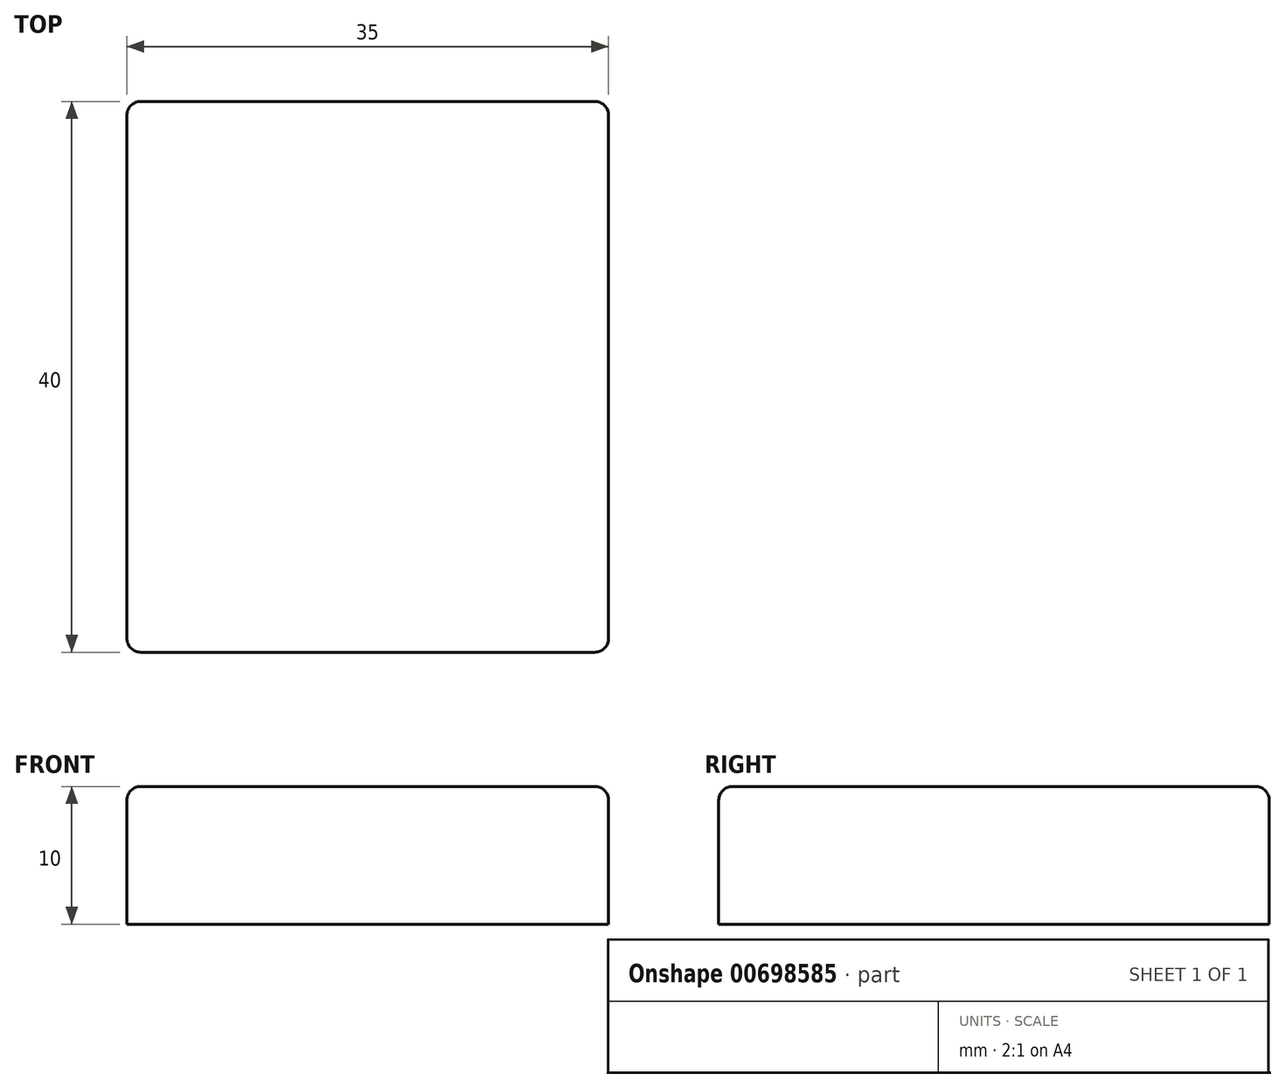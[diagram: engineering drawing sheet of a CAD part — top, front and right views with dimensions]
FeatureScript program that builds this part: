
annotation { "Feature Type Name" : "Feature", "Feature Type Description" : "" }
export const myFeature = defineFeature(function(context is Context, id is Id, definition is map)
    precondition{}
    {
        {
            var Q0;
            Q0=qCreatedBy(makeId("Top.planeOp"),FACE);
            var sketch = newSketch(context, id + "F0", { "sketchPlane" : qUnion([Q0])});
            skLineSegment(sketch, "E0.top", {"start": v(-17.5, -20) * mm, "end": v(17.5, -20) * mm});
            skLineSegment(sketch, "E0.left", {"start": v(-17.5, 20) * mm, "end": v(-17.5, -20) * mm});
            skLineSegment(sketch, "E1.MirrorCS", {"start": v(17.5, 20) * mm, "end": v(17.5, -20) * mm});
            skLineSegment(sketch, "E2.MirrorCS", {"start": v(-17.5, 20) * mm, "end": v(17.5, 20) * mm});
            skSolve(sketch);
        }
        {
            var Q0;
            Q0=qSketchRegion(id+"F0",true);
            extrude(context, id + "F1", {"entities" : qUnion([Q0]), "flatOperationType" : FlatOperationType.REMOVE, "depth" : 10 * mm, "offsetDistance" : 25 * mm, "domain" : OperationDomain.MODEL});
        }
        {
            var Q0;
            Q0=makeQuery(id+"F1.opExtrude","CAP_EDGE",EDGE,{"disambiguationData":[OSD([sQuery(id+"F0.wireOp",EDGE,"E2.MirrorCS")])],"isStart":false});
            var Q1;
            Q1=makeQuery(id+"F1.opExtrude","CAP_EDGE",EDGE,{"disambiguationData":[OSD([sQuery(id+"F0.wireOp",EDGE,"E1.MirrorCS")])],"isStart":false});
            var Q2;
            Q2=makeQuery(id+"F1.opExtrude","CAP_EDGE",EDGE,{"disambiguationData":[OSD([sQuery(id+"F0.wireOp",EDGE,"E0.top")])],"isStart":false});
            var Q3;
            Q3=makeQuery(id+"F1.opExtrude","CAP_EDGE",EDGE,{"disambiguationData":[OSD([sQuery(id+"F0.wireOp",EDGE,"E0.left")])],"isStart":false});
            var Q4;
            Q4=makeQuery(id+"Ft5btwJ2Vh0EV5n_1.boolean.opBoolean","MERGE",EDGE,{"derivedFrom":[makeQuery(id+"F1.opExtrude","SWEPT_EDGE",EDGE,{"disambiguationData":[OSD([sQuery(id+"F0.wireOp",EDGE,"E0.top"),sQuery(id+"F0.wireOp",EDGE,"E1.MirrorCS")])]}),makeQuery(id+"Ft5btwJ2Vh0EV5n_1.opExtrude","SWEPT_EDGE",EDGE,{"disambiguationData":[OSD([sQuery(id+"FW4ArBo40ERr3nP_1.wireOp",EDGE,"Kx4ZLxtj-8PWd-bxCC-HsaW-OyicG5s6qaQg.top"),sQuery(id+"FW4ArBo40ERr3nP_1.wireOp",EDGE,"Kx4ZLxtj-8PWd-bxCC-HsaW-OyicG5s6qaQg.right")])]})]});
            var Q5;
            Q5=makeQuery(id+"Ft5btwJ2Vh0EV5n_1.boolean.opBoolean","MERGE",EDGE,{"derivedFrom":[makeQuery(id+"F1.opExtrude","SWEPT_EDGE",EDGE,{"disambiguationData":[OSD([sQuery(id+"F0.wireOp",EDGE,"E0.top"),sQuery(id+"F0.wireOp",EDGE,"E0.left")])]}),makeQuery(id+"Ft5btwJ2Vh0EV5n_1.opExtrude","SWEPT_EDGE",EDGE,{"disambiguationData":[OSD([sQuery(id+"FW4ArBo40ERr3nP_1.wireOp",EDGE,"Kx4ZLxtj-8PWd-bxCC-HsaW-OyicG5s6qaQg.top"),sQuery(id+"FW4ArBo40ERr3nP_1.wireOp",EDGE,"Kx4ZLxtj-8PWd-bxCC-HsaW-OyicG5s6qaQg.left")])]})]});
            var Q6;
            Q6=makeQuery(id+"Ft5btwJ2Vh0EV5n_1.boolean.opBoolean","MERGE",EDGE,{"derivedFrom":[makeQuery(id+"F1.opExtrude","SWEPT_EDGE",EDGE,{"disambiguationData":[OSD([sQuery(id+"F0.wireOp",EDGE,"E0.left"),sQuery(id+"F0.wireOp",EDGE,"E2.MirrorCS")])]}),makeQuery(id+"Ft5btwJ2Vh0EV5n_1.opExtrude","SWEPT_EDGE",EDGE,{"disambiguationData":[OSD([sQuery(id+"FW4ArBo40ERr3nP_1.wireOp",EDGE,"Kx4ZLxtj-8PWd-bxCC-HsaW-OyicG5s6qaQg.bottom"),sQuery(id+"FW4ArBo40ERr3nP_1.wireOp",EDGE,"Kx4ZLxtj-8PWd-bxCC-HsaW-OyicG5s6qaQg.left")])]})]});
            var Q7;
            Q7=makeQuery(id+"Ft5btwJ2Vh0EV5n_1.boolean.opBoolean","MERGE",EDGE,{"derivedFrom":[makeQuery(id+"F1.opExtrude","SWEPT_EDGE",EDGE,{"disambiguationData":[OSD([sQuery(id+"F0.wireOp",EDGE,"E1.MirrorCS"),sQuery(id+"F0.wireOp",EDGE,"E2.MirrorCS")])]}),makeQuery(id+"Ft5btwJ2Vh0EV5n_1.opExtrude","SWEPT_EDGE",EDGE,{"disambiguationData":[OSD([sQuery(id+"FW4ArBo40ERr3nP_1.wireOp",EDGE,"Kx4ZLxtj-8PWd-bxCC-HsaW-OyicG5s6qaQg.bottom"),sQuery(id+"FW4ArBo40ERr3nP_1.wireOp",EDGE,"Kx4ZLxtj-8PWd-bxCC-HsaW-OyicG5s6qaQg.right")])]})]});
            fillet(context, id + "F2", {"entities" : qUnion([Q0, Q1, Q2, Q3, Q4, Q5, Q6, Q7]), "radius" : 1 * mm, "tangentPropagation" : true, "allowEdgeOverflow" : false});
        }
    });
